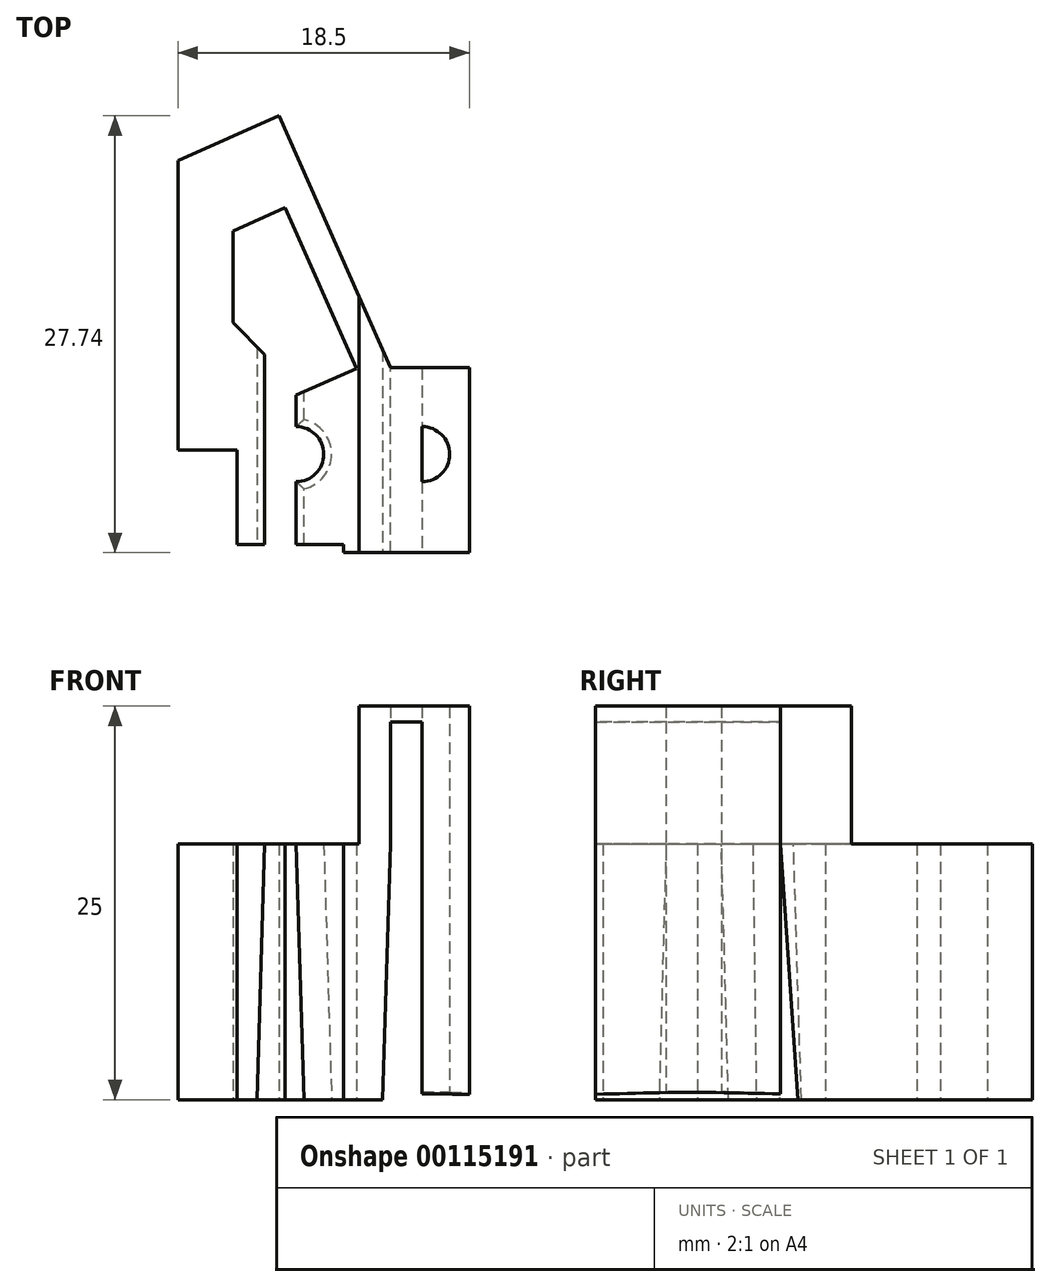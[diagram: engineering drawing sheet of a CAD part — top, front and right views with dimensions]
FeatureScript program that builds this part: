
annotation { "Feature Type Name" : "Feature", "Feature Type Description" : "" }
export const myFeature = defineFeature(function(context is Context, id is Id, definition is map)
    precondition{}
    {
        {
            var Q0;
            Q0=qCreatedBy(makeId("Top.planeOp"),FACE);
            var sketch = newSketch(context, id + "F0", { "sketchPlane" : qUnion([Q0])});
            skLineSegment(sketch, "E0", {"start": v(-7, -5.75) * mm, "end": v(-7, 6.34) * mm});
            skLineSegment(sketch, "E1", {"start": v(-7, 6.34) * mm, "end": v(-9.02, 8.36) * mm});
            skLineSegment(sketch, "E2", {"start": v(-9.02, 8.36) * mm, "end": v(-9.02, 14.18) * mm});
            skLineSegment(sketch, "E3", {"start": v(-9.02, 14.18) * mm, "end": v(-5.7, 15.66) * mm});
            skLineSegment(sketch, "E4", {"start": v(-5.7, 15.66) * mm, "end": v(-1.17, 5.45) * mm});
            skLineSegment(sketch, "E5", {"start": v(-1.17, 5.45) * mm, "end": v(-5, 3.75) * mm});
            skLineSegment(sketch, "E6", {"start": v(-5, 3.75) * mm, "end": v(-5, 1.75) * mm});
            skArc(sketch, "E7", {"start": v(-5, 1.75) * mm, "mid": v(-3.76, 1.24) * mm, "end": v(-3.25, 0) * mm});
            skArc(sketch, "E8", {"start": v(-3.25, 0) * mm, "mid": v(-3.76, -1.24) * mm, "end": v(-5, -1.75) * mm});
            skLineSegment(sketch, "E9", {"start": v(-5, -1.75) * mm, "end": v(-5, -5.75) * mm});
            skLineSegment(sketch, "E10", {"start": v(-5, -5.75) * mm, "end": v(-2, -5.75) * mm});
            skLineSegment(sketch, "E11", {"start": v(-2, -5.75) * mm, "end": v(-2, -6.25) * mm});
            skLineSegment(sketch, "E12", {"start": v(-2, -6.25) * mm, "end": v(1, -6.25) * mm});
            skLineSegment(sketch, "E13", {"start": v(1, -6.25) * mm, "end": v(1, 5.5) * mm});
            skLineSegment(sketch, "E14", {"start": v(1, 5.5) * mm, "end": v(-6.1, 21.5) * mm});
            skLineSegment(sketch, "E15", {"start": v(-6.1, 21.5) * mm, "end": v(-12.5, 18.65) * mm});
            skLineSegment(sketch, "E16", {"start": v(-12.5, 18.65) * mm, "end": v(-12.5, 0.25) * mm});
            skLineSegment(sketch, "E17", {"start": v(-12.5, 0.25) * mm, "end": v(-8.75, 0.25) * mm});
            skLineSegment(sketch, "E18", {"start": v(-8.75, 0.25) * mm, "end": v(-8.75, -5.75) * mm});
            skLineSegment(sketch, "E19", {"start": v(-8.75, -5.75) * mm, "end": v(-7, -5.75) * mm});
            skLineSegment(sketch, "E20", {"start": v(-1, -6.25) * mm, "end": v(-1, 10) * mm});
            skLineSegment(sketch, "E21", {"start": v(1, 5.5) * mm, "end": v(3, 5.5) * mm});
            skLineSegment(sketch, "E22", {"start": v(3, 5.5) * mm, "end": v(3, -6.25) * mm});
            skLineSegment(sketch, "E23", {"start": v(3, -6.25) * mm, "end": v(1, -6.25) * mm});
            skLineSegment(sketch, "E24", {"start": v(3, -6.25) * mm, "end": v(6, -6.25) * mm});
            skLineSegment(sketch, "E25", {"start": v(6, -6.25) * mm, "end": v(6, 5.5) * mm});
            skLineSegment(sketch, "E26", {"start": v(6, 5.5) * mm, "end": v(3, 5.5) * mm});
            skArc(sketch, "E27", {"start": v(3, 1.75) * mm, "mid": v(4.75, 0) * mm, "end": v(3, -1.75) * mm});
            skSolve(sketch);
        }
        {
            var Q0;
            Q0=makeQuery(id+"F0.imprint","IMPRINT",FACE,{"disambiguationData":[TD([[makeQuery(id+"F0.imprint","IMPRINT",EDGE,{"derivedFrom":sQuery(id+"F0.wireOp",EDGE,"E0")}),1.0]])]});
            extrude(context, id + "F1", {"entities" : qUnion([Q0]), "depth" : 16.25 * mm});
        }
        {
            var Q0;
            {var subQ0=sQuery(id+"F0.wireOp",EDGE,"E13");Q0=makeQuery(id+"F0.imprint","IMPRINT",FACE,{"disambiguationData":[TD([[makeQuery(id+"F0.imprint","IMPRINT",EDGE,{"derivedFrom":subQ0}),1.0]])]});}
            var Q1;
            {var subQ0=sQuery(id+"F0.wireOp",EDGE,"E24");Q1=makeQuery(id+"F0.imprint","IMPRINT",FACE,{"disambiguationData":[TD([[makeQuery(id+"F0.imprint","IMPRINT",EDGE,{"derivedFrom":subQ0}),1.0]])]});}
            extrude(context, id + "F2", {"entities" : qUnion([Q0, Q1]), "operationType" : NewBodyOperationType.ADD, "depth" : 25 * mm});
        }
        {
            var Q0;
            Q0=makeQuery(id+"F0.imprint","IMPRINT",FACE,{"disambiguationData":[TD([[makeQuery(id+"F0.imprint","IMPRINT",EDGE,{"derivedFrom":sQuery(id+"F0.wireOp",EDGE,"E13")}),-1.0]])]});
            extrude(context, id + "F3", {"entities" : qUnion([Q0]), "operationType" : NewBodyOperationType.ADD, "depth" : 25 * mm, "hasSecondDirection" : true, "secondDirectionOppositeDirection" : false, "secondDirectionDepth" : 24 * mm});
        }
        {
            var Q0;
            {var subQ0=sQuery(id+"F0.wireOp",EDGE,"E27");Q0=makeQuery(id+"F0.imprint","IMPRINT",FACE,{"disambiguationData":[TD([[makeQuery(id+"F0.imprint","IMPRINT",EDGE,{"derivedFrom":subQ0}),-1.0]])]});}
            extrude(context, id + "F4", {"entities" : qUnion([Q0]), "operationType" : NewBodyOperationType.ADD, "depth" : 25 * mm, "hasSecondDirection" : true, "secondDirectionOppositeDirection" : false, "secondDirectionDepth" : 17 * mm});
        }
        {
            var Q0;
            Q0=makeQuery(id+"F1.opExtrude","CAP_EDGE",EDGE,{"disambiguationData":[OSD([sQuery(id+"F0.wireOp",EDGE,"E0")])],"isStart":true});
            var Q1;
            Q1=makeQuery(id+"F1.opExtrude","CAP_EDGE",EDGE,{"disambiguationData":[OSD([sQuery(id+"F0.wireOp",EDGE,"E9")])],"isStart":true});
            var Q2;
            Q2=makeQuery(id+"F1.opExtrude","CAP_EDGE",EDGE,{"disambiguationData":[OSD([sQuery(id+"F0.wireOp",EDGE,"E6")])],"isStart":true});
            var Q3;
            Q3=makeQuery(id+"F1.opExtrude","CAP_EDGE",EDGE,{"disambiguationData":[OSD([sQuery(id+"F0.wireOp",EDGE,"E7"),sQuery(id+"F0.wireOp",EDGE,"E8")])],"isStart":true});
            var Q4;
            {var subQ0=sQuery(id+"F0.wireOp",EDGE,"E22");Q4=makeQuery(id+"F2.opExtrude","CAP_EDGE",EDGE,{"disambiguationData":[OSD([subQ0]),TDD([makeQuery(id+"F0.imprint","IMPRINT",EDGE,{"disambiguationData":[TD([[makeQuery(id+"F0.imprint","INTERSECT",VERTEX,{"disambiguationData":[OD(0.0)],"derivedFrom":[subQ0,sQuery(id+"F0.wireOp",EDGE,"E27")]}),1.0]])],"derivedFrom":subQ0})])],"isStart":true});}
            var Q5;
            Q5=makeQuery(id+"F2.opExtrude","CAP_EDGE",EDGE,{"disambiguationData":[OSD([sQuery(id+"F0.wireOp",EDGE,"E13")])],"isStart":true});
            var Q6;
            {var subQ0=sQuery(id+"F0.wireOp",EDGE,"E22");Q6=makeQuery(id+"F2.opExtrude","CAP_EDGE",EDGE,{"disambiguationData":[OSD([subQ0]),TDD([makeQuery(id+"F0.imprint","IMPRINT",EDGE,{"disambiguationData":[TD([[makeQuery(id+"F0.imprint","INTERSECT",VERTEX,{"disambiguationData":[OD(1.0)],"derivedFrom":[subQ0,sQuery(id+"F0.wireOp",EDGE,"E27")]}),-1.0]])],"derivedFrom":subQ0})])],"isStart":true});}
            var Q7;
            Q7=makeQuery(id+"F2.opExtrude","CAP_EDGE",EDGE,{"disambiguationData":[OSD([sQuery(id+"F0.wireOp",EDGE,"E27")])],"isStart":true});
            chamfer(context, id + "F5", {"entities" : qUnion([Q0, Q1, Q2, Q3, Q4, Q5, Q6, Q7]), "chamferType" : ChamferType.TWO_OFFSETS, "width1" : 16.25 * mm, "oppositeDirection" : false, "width2" : .5 * mm, "tangentPropagation" : true});
        }
    });
